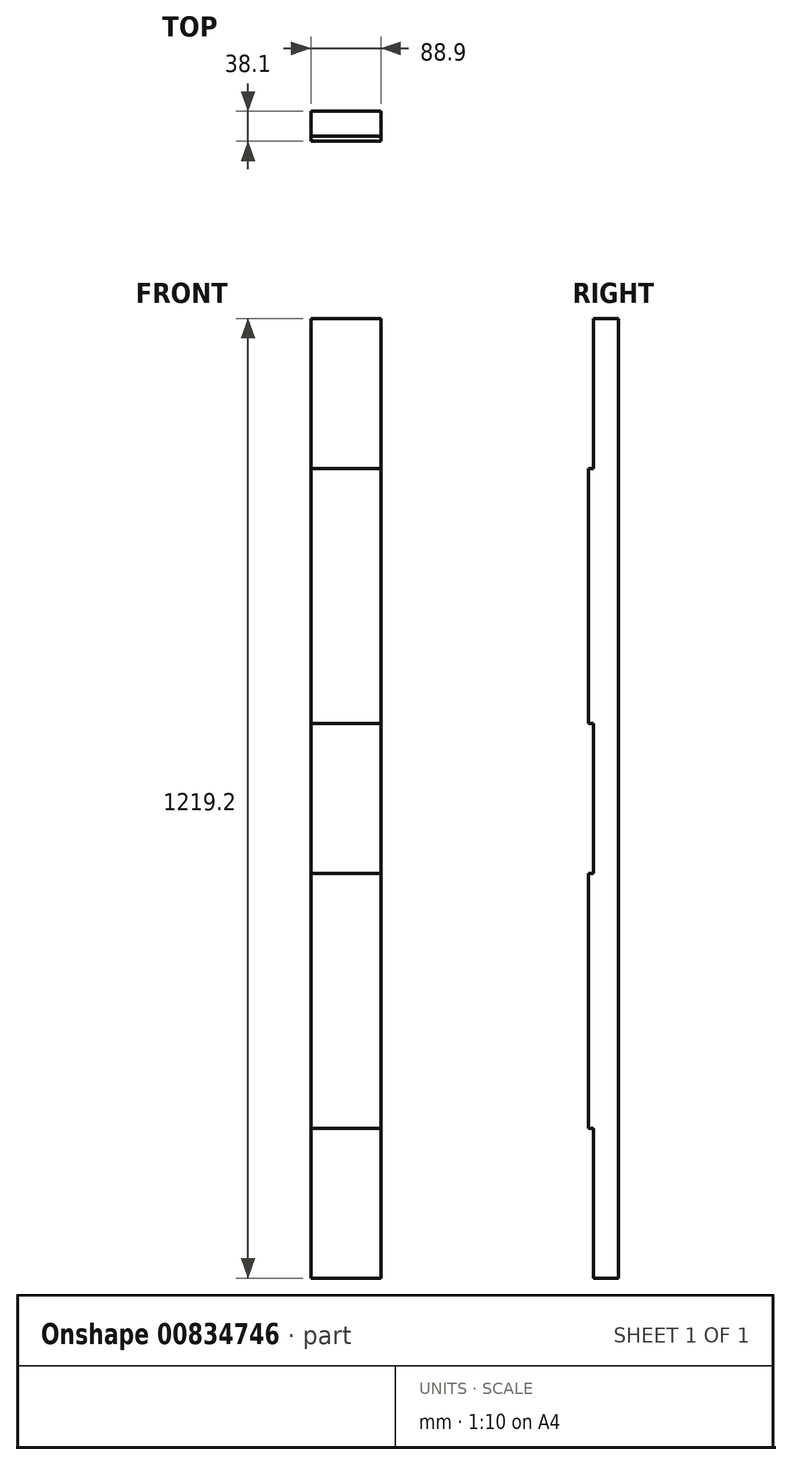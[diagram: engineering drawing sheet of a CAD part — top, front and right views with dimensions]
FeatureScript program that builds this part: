
annotation { "Feature Type Name" : "Feature", "Feature Type Description" : "" }
export const myFeature = defineFeature(function(context is Context, id is Id, definition is map)
    precondition{}
    {
        {
            var Q0;
            Q0=qCreatedBy(makeId("Front.planeOp"),FACE);
            var sketch = newSketch(context, id + "F0", { "sketchPlane" : qUnion([Q0])});
            skLineSegment(sketch, "E0.bottom", {"start": v(44.45, -609.6) * mm, "end": v(-44.45, -609.6) * mm});
            skLineSegment(sketch, "E0.top", {"start": v(44.45, 609.6) * mm, "end": v(-44.45, 609.6) * mm});
            skLineSegment(sketch, "E0.left", {"start": v(44.45, -609.6) * mm, "end": v(44.45, 609.6) * mm});
            skLineSegment(sketch, "E0.right", {"start": v(-44.45, -609.6) * mm, "end": v(-44.45, 609.6) * mm});
            skPoint(sketch, "E0.middle", {"position": v(0, 0) * mm});
            skSolve(sketch);
        }
        {
            var Q0;
            Q0 = qSketchRegion(id + "F0", true);
            extrude(context, id + "F1", {"entities" : qUnion([Q0]), "endBound" : BoundingType.SYMMETRIC, "depth" : 38.1 * mm, "offsetDistance" : 25.4 * mm});
        }
        {
            var Q0;
            Q0=makeQuery(id+"F1.opExtrude","CAP_FACE",FACE,{"disambiguationData":[OSD([sQuery(id+"F0.wireOp",EDGE,"E0.bottom"),sQuery(id+"F0.wireOp",EDGE,"E0.top"),sQuery(id+"F0.wireOp",EDGE,"E0.left"),sQuery(id+"F0.wireOp",EDGE,"E0.right")])],"isStart":false});
            var sketch = newSketch(context, id + "F2", { "sketchPlane" : qUnion([Q0])});
            skLineSegment(sketch, "E1.bottom", {"start": v(44.45, -95.25) * mm, "end": v(-44.45, -95.25) * mm});
            skLineSegment(sketch, "E1.top", {"start": v(44.45, 95.25) * mm, "end": v(-44.45, 95.25) * mm});
            skLineSegment(sketch, "E1.left", {"start": v(44.45, -95.25) * mm, "end": v(44.45, 95.25) * mm});
            skLineSegment(sketch, "E1.right", {"start": v(-44.45, -95.25) * mm, "end": v(-44.45, 95.25) * mm});
            skPoint(sketch, "E1.middle", {"position": v(0, 0) * mm});
            skLineSegment(sketch, "E2.bottom", {"start": v(-44.45, 609.6) * mm, "end": v(44.45, 609.6) * mm});
            skLineSegment(sketch, "E2.top", {"start": v(-44.45, 419.1) * mm, "end": v(44.45, 419.1) * mm});
            skLineSegment(sketch, "E2.left", {"start": v(-44.45, 609.6) * mm, "end": v(-44.45, 419.1) * mm});
            skLineSegment(sketch, "E2.right", {"start": v(44.45, 609.6) * mm, "end": v(44.45, 419.1) * mm});
            skLineSegment(sketch, "E3", {"start": v(-44.45, 419.1) * mm, "end": v(-44.45, 95.25) * mm});
            skLineSegment(sketch, "E4.bottom", {"start": v(44.45, 234.95) * mm, "end": v(-44.45, 234.95) * mm});
            skLineSegment(sketch, "E4.top", {"start": v(44.45, 279.4) * mm, "end": v(-44.45, 279.4) * mm});
            skLineSegment(sketch, "E4.left", {"start": v(44.45, 234.95) * mm, "end": v(44.45, 279.4) * mm});
            skLineSegment(sketch, "E4.right", {"start": v(-44.45, 234.95) * mm, "end": v(-44.45, 279.4) * mm});
            skPoint(sketch, "E4.middle", {"position": v(0, 257.18) * mm});
            skPoint(sketch, "E4.middle.positionSnap0", {"position": v(-44.45, 257.18) * mm});
            skPoint(sketch, "E4.centerSnap0", {"position": v(-44.45, 257.18) * mm});
            skLineSegment(sketch, "E5", {"start": v(-44.45, 234.95) * mm, "end": v(-44.45, 95.25) * mm});
            skLineSegment(sketch, "E6.bottom", {"start": v(44.45, 187.33) * mm, "end": v(-44.45, 187.33) * mm});
            skLineSegment(sketch, "E6.top", {"start": v(44.45, 142.88) * mm, "end": v(-44.45, 142.88) * mm});
            skLineSegment(sketch, "E6.left", {"start": v(44.45, 187.33) * mm, "end": v(44.45, 142.88) * mm});
            skLineSegment(sketch, "E6.right", {"start": v(-44.45, 187.33) * mm, "end": v(-44.45, 142.88) * mm});
            skPoint(sketch, "E6.middle", {"position": v(0, 165.1) * mm});
            skPoint(sketch, "E6.middle.positionSnap0", {"position": v(-44.45, 165.1) * mm});
            skPoint(sketch, "E6.centerSnap0", {"position": v(-44.45, 165.1) * mm});
            skLineSegment(sketch, "E7", {"start": v(-44.45, 257.18) * mm, "end": v(0, 257.18) * mm});
            skPoint(sketch, "E8.MirrorP", {"position": v(-44.45, 349.25) * mm});
            skLineSegment(sketch, "E9.MirrorCS", {"start": v(44.45, 327.03) * mm, "end": v(44.45, 371.48) * mm});
            skLineSegment(sketch, "E10.MirrorCS", {"start": v(-44.45, 327.03) * mm, "end": v(-44.45, 371.48) * mm});
            skPoint(sketch, "E11.MirrorP", {"position": v(0, 349.25) * mm});
            skLineSegment(sketch, "E12.MirrorCS", {"start": v(44.45, 371.48) * mm, "end": v(-44.45, 371.48) * mm});
            skLineSegment(sketch, "E13.MirrorCS", {"start": v(44.45, 327.03) * mm, "end": v(-44.45, 327.03) * mm});
            skLineSegment(sketch, "E14.MirrorCS", {"start": v(44.45, -187.33) * mm, "end": v(44.45, -142.88) * mm});
            skLineSegment(sketch, "E15.MirrorCS", {"start": v(-44.45, -234.95) * mm, "end": v(-44.45, -279.4) * mm});
            skLineSegment(sketch, "E16.MirrorCS", {"start": v(-44.45, -419.1) * mm, "end": v(-44.45, -95.25) * mm});
            skLineSegment(sketch, "E17.MirrorCS", {"start": v(-44.45, -187.33) * mm, "end": v(-44.45, -142.88) * mm});
            skLineSegment(sketch, "E18.MirrorCS", {"start": v(-44.45, -234.95) * mm, "end": v(-44.45, -95.25) * mm});
            skLineSegment(sketch, "E19.MirrorCS", {"start": v(44.45, -327.03) * mm, "end": v(44.45, -371.48) * mm});
            skLineSegment(sketch, "E20.MirrorCS", {"start": v(44.45, -234.95) * mm, "end": v(44.45, -279.4) * mm});
            skLineSegment(sketch, "E21.MirrorCS", {"start": v(-44.45, -327.03) * mm, "end": v(-44.45, -371.48) * mm});
            skLineSegment(sketch, "E22.MirrorCS", {"start": v(-44.45, -257.18) * mm, "end": v(0, -257.18) * mm});
            skPoint(sketch, "E23.MirrorP", {"position": v(-44.45, -257.18) * mm});
            skLineSegment(sketch, "E24.MirrorCS", {"start": v(44.45, -187.33) * mm, "end": v(-44.45, -187.33) * mm});
            skLineSegment(sketch, "E25.MirrorCS", {"start": v(44.45, -142.88) * mm, "end": v(-44.45, -142.88) * mm});
            skLineSegment(sketch, "E26.MirrorCS", {"start": v(44.45, -234.95) * mm, "end": v(-44.45, -234.95) * mm});
            skPoint(sketch, "E27.MirrorP", {"position": v(-44.45, -349.25) * mm});
            skLineSegment(sketch, "E28.MirrorCS", {"start": v(44.45, -327.03) * mm, "end": v(-44.45, -327.03) * mm});
            skLineSegment(sketch, "E29.MirrorCS", {"start": v(44.45, -371.48) * mm, "end": v(-44.45, -371.48) * mm});
            skPoint(sketch, "E30.MirrorP", {"position": v(-44.45, -165.1) * mm});
            skLineSegment(sketch, "E31.MirrorCS", {"start": v(44.45, -279.4) * mm, "end": v(-44.45, -279.4) * mm});
            skLineSegment(sketch, "E32.MirrorCS", {"start": v(44.45, -609.6) * mm, "end": v(44.45, -419.1) * mm});
            skPoint(sketch, "E33.MirrorP", {"position": v(0, -349.25) * mm});
            skLineSegment(sketch, "E34.MirrorCS", {"start": v(-44.45, 95.25) * mm, "end": v(-44.45, -95.25) * mm});
            skLineSegment(sketch, "E35.MirrorCS", {"start": v(44.45, 95.25) * mm, "end": v(44.45, -95.25) * mm});
            skLineSegment(sketch, "E36.MirrorCS", {"start": v(-44.45, -609.6) * mm, "end": v(-44.45, -419.1) * mm});
            skLineSegment(sketch, "E37.MirrorCS", {"start": v(-44.45, -419.1) * mm, "end": v(44.45, -419.1) * mm});
            skPoint(sketch, "E38.MirrorP", {"position": v(0, -257.18) * mm});
            skLineSegment(sketch, "E39.MirrorCS", {"start": v(-44.45, -609.6) * mm, "end": v(44.45, -609.6) * mm});
            skPoint(sketch, "E40.MirrorP", {"position": v(0, -165.1) * mm});
            skSolve(sketch);
        }
        {
            var Q0;
            Q0=makeQuery(id+"F2.imprint","IMPRINT",FACE,{"disambiguationData":[TD([[makeQuery(id+"F2.imprint","IMPRINT",EDGE,{"derivedFrom":sQuery(id+"F2.wireOp",EDGE,"E32.MirrorCS")}),1.0]])]});
            var Q1;
            Q1=makeQuery(id+"F2.imprint","IMPRINT",FACE,{"disambiguationData":[TD([[makeQuery(id+"F2.imprint","IMPRINT",EDGE,{"derivedFrom":sQuery(id+"F2.wireOp",EDGE,"E1.top")}),1.0]])]});
            var Q2;
            Q2=makeQuery(id+"F2.imprint","IMPRINT",FACE,{"disambiguationData":[TD([[makeQuery(id+"F2.imprint","IMPRINT",EDGE,{"derivedFrom":sQuery(id+"F2.wireOp",EDGE,"E2.bottom")}),1.0]])]});
            extrude(context, id + "F3", {"entities" : qUnion([Q0, Q1, Q2]), "operationType" : NewBodyOperationType.REMOVE, "oppositeDirection" : true, "depth" : 6.35 * mm, "offsetDistance" : 25.4 * mm});
        }
    });
